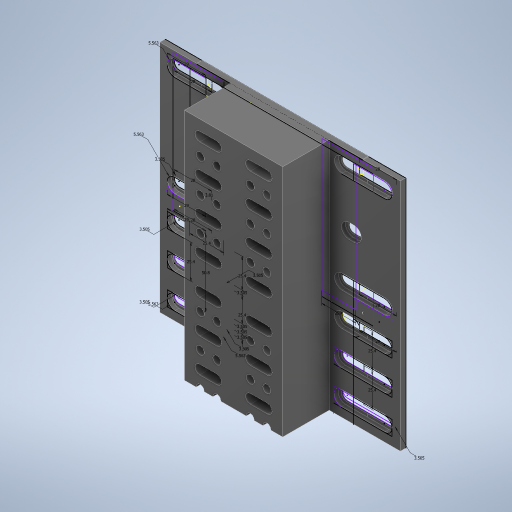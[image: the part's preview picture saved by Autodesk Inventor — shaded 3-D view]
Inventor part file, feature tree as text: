
AUTODESK INVENTOR PART (.ipt)
format: ipt  version: 2024.2 (Build 282272000, 272)  size: 1,234,944 bytes
history: native  units: in
note: dims shown in document units (in); Inventor stores cm internally (conversion verified against a paired STEP export)
features: extrude x9, sketch x7, direct_edit x6, other x4, move_body x4, thicken_offset x2, mirror x1
ambient origin geometry x8: Origin, YZ Plane, XZ Plane, XY Plane, X Axis, Y Axis, Z Axis, Center Point
bodies: Solid1 (feature_tree)
feature tree (33):
  other  "LS-5012 - LS-BREADBOARD ADAPTER PLATE (CATALOG MODEL).SAT"
  sketch  "Sketch1"  dims[d0=1.0in d1=1.0in]
  extrude  "Extrusion1"  Depth=1.0in
  thicken_offset  "Thicken1"
  direct_edit  "Direct Edit3"
  mirror  "Mirror3"
  extrude  "Extrusion5"  Depth=0.1in
  extrude  "Extrusion6"  Depth=0.01in TaperAngle=0.0deg
  sketch  "Sketch6"  dims[d28=0.956in d29=0.0in d30=0.175in d31=0.0in]
  extrude  "Extrusion7"  Depth=0.175in TaperAngle=0.0deg
  sketch  "Sketch7"  dims[d32=1.1024in d33=1.1024in]
  extrude  "Extrusion8"  Depth=1.1024in
  direct_edit  "Direct Edit6"
  direct_edit  "Direct Edit7"
  direct_edit  "Direct Edit8"
  extrude  "Extrusion9"  Depth=1.1024in
  thicken_offset  "Thicken2"
  direct_edit  "Direct Edit9"
  extrude  "Extrusion10"  Depth=0.138in
  extrude  "Extrusion11"  Depth=1.1024in
  extrude  "Extrusion12"  Depth=1.1024in
  direct_edit  "Direct Edit10"
  sketch  "Sketch9"  dims[d36=0.15in d37=0.138in d38=1.1024in d39=1.1024in d40=1.0in d41=1.0in d42=1.0in d43=1.0in d44=0.138in d45=0.138in d46=0.138in d47=0.138in d48=0.138in d49=0.138in d50=0.138in d51=0.175in d52=0.0in d53=1.1417in d54=0.219in d55=1.1417in d56=1.1417in d57=0.7874in d59=1.0in d60=0.3937in d62=1.0in d64=0.138in d65=0.138in d66=0.7874in d68=2.0in d69=0.3937in d71=1.0in d73=0.219in d74=0.219in d75=0.06in d76=0.0in d77=0.219in d80=-0.0787in d81=1.0626in d82=0.0in d83=0.0in d84=-0.0066in d85=1.1024in d86=0.1575in d87=0.0in d88=0.0394in d89=0.0394in d90=0.0612in d91=0.1969in d92=0.0in d93=0.1378in d94=0.0in d95=0.1378in d96=0.0in d97=0.0in d98=0.0in d99=-0.0394in]
  sketch  "Sketch4"  dims[d2=0.2in d3=0.0in d14=0.1in d15=3.0in]
  sketch  "Sketch5"  dims[d22=0.0in d23=0.0in d24=0.0345in d25=0.0in d26=0.0in d27=0.01in]
  sketch  "Sketch8"  dims[d34=1.1024in d35=1.1024in]
  move_body  "Move3"
  move_body  "Move4"
  other  "Size3"
  other  "Size4"
  move_body  "Move5"
  other  "Size5"
  move_body  "Move6"
